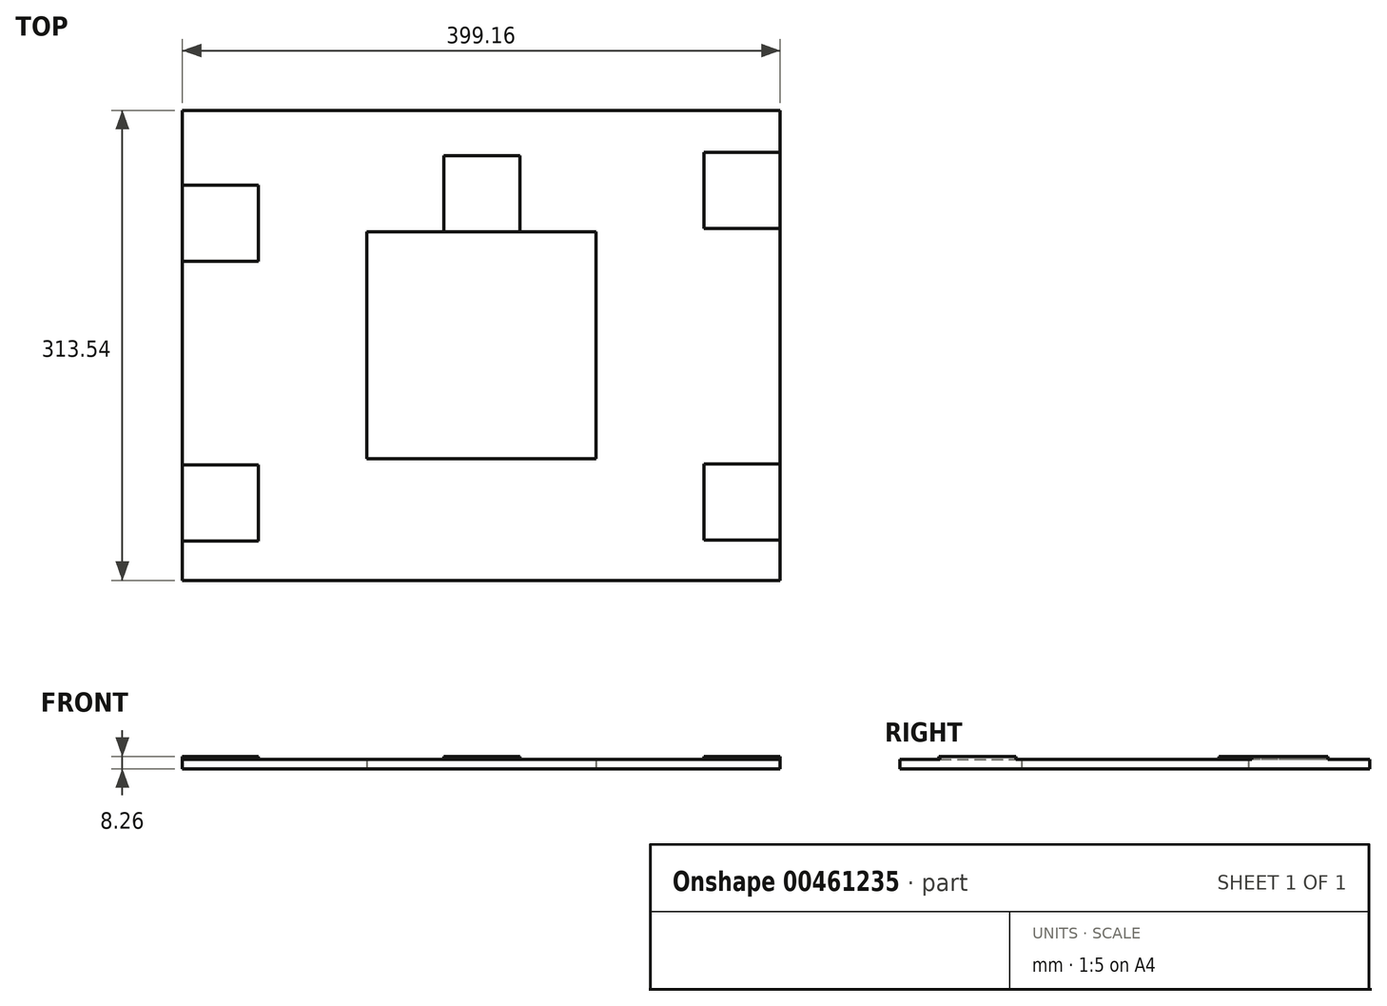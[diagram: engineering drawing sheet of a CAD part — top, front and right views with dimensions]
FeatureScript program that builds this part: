
annotation { "Feature Type Name" : "Feature", "Feature Type Description" : "" }
export const myFeature = defineFeature(function(context is Context, id is Id, definition is map)
    precondition{}
    {
        {
            var Q0;
            Q0=qCreatedBy(makeId("Top.planeOp"),FACE);
            var sketch = newSketch(context, id + "F0", { "sketchPlane" : qUnion([Q0])});
            skLineSegment(sketch, "E0.bottom", {"start": v(199.58, 156.77) * mm, "end": v(-199.58, 156.77) * mm});
            skLineSegment(sketch, "E0.top", {"start": v(199.58, -156.77) * mm, "end": v(-199.58, -156.77) * mm});
            skLineSegment(sketch, "E0.left", {"start": v(199.58, 156.77) * mm, "end": v(199.58, -156.77) * mm});
            skLineSegment(sketch, "E0.right", {"start": v(-199.58, 156.77) * mm, "end": v(-199.58, -156.77) * mm});
            skPoint(sketch, "E0.middle", {"position": v(0, 0) * mm});
            skLineSegment(sketch, "E1.bottom", {"start": v(76.5, 75.74) * mm, "end": v(-76.5, 75.74) * mm});
            skLineSegment(sketch, "E1.top", {"start": v(76.5, -75.74) * mm, "end": v(-76.5, -75.74) * mm});
            skLineSegment(sketch, "E1.left", {"start": v(76.5, 75.74) * mm, "end": v(76.5, -75.74) * mm});
            skLineSegment(sketch, "E1.right", {"start": v(-76.5, 75.74) * mm, "end": v(-76.5, -75.74) * mm});
            skSolve(sketch);
        }
        {
            var Q0;
            Q0=makeQuery(id+"F0.imprint","IMPRINT",FACE,{"disambiguationData":[TD([[makeQuery(id+"F0.imprint","IMPRINT",EDGE,{"derivedFrom":sQuery(id+"F0.wireOp",EDGE,"E0.bottom")}),1.0]])]});
            extrude(context, id + "F1", {"entities" : qUnion([Q0]), "depth" : 6.35 * mm});
        }
        {
            var Q0;
            Q0=makeQuery(id+"F1.opExtrude","CAP_FACE",FACE,{"disambiguationData":[OSD([sQuery(id+"F0.wireOp",EDGE,"E0.bottom"),sQuery(id+"F0.wireOp",EDGE,"E0.top"),sQuery(id+"F0.wireOp",EDGE,"E0.left"),sQuery(id+"F0.wireOp",EDGE,"E0.right"),sQuery(id+"F0.wireOp",EDGE,"E1.bottom"),sQuery(id+"F0.wireOp",EDGE,"E1.top"),sQuery(id+"F0.wireOp",EDGE,"E1.left"),sQuery(id+"F0.wireOp",EDGE,"E1.right")])],"isStart":false});
            var sketch = newSketch(context, id + "F2", { "sketchPlane" : qUnion([Q0])});
            skLineSegment(sketch, "E2.bottom", {"start": v(-199.58, 106.93) * mm, "end": v(-148.78, 106.93) * mm});
            skLineSegment(sketch, "E2.top", {"start": v(-199.58, 56.13) * mm, "end": v(-148.78, 56.13) * mm});
            skLineSegment(sketch, "E2.left", {"start": v(-199.58, 106.93) * mm, "end": v(-199.58, 56.13) * mm});
            skLineSegment(sketch, "E2.right", {"start": v(-148.78, 106.93) * mm, "end": v(-148.78, 56.13) * mm});
            skLineSegment(sketch, "E3.bottom", {"start": v(199.58, 128.8) * mm, "end": v(148.78, 128.8) * mm});
            skLineSegment(sketch, "E3.top", {"start": v(199.58, 78) * mm, "end": v(148.78, 78) * mm});
            skLineSegment(sketch, "E3.left", {"start": v(199.58, 128.8) * mm, "end": v(199.58, 78) * mm});
            skLineSegment(sketch, "E3.right", {"start": v(148.78, 128.8) * mm, "end": v(148.78, 78) * mm});
            skLineSegment(sketch, "E4.bottom", {"start": v(199.58, -130.05) * mm, "end": v(148.78, -130.05) * mm});
            skLineSegment(sketch, "E4.top", {"start": v(199.58, -79.25) * mm, "end": v(148.78, -79.25) * mm});
            skLineSegment(sketch, "E4.left", {"start": v(199.58, -130.05) * mm, "end": v(199.58, -79.25) * mm});
            skLineSegment(sketch, "E4.right", {"start": v(148.78, -130.05) * mm, "end": v(148.78, -79.25) * mm});
            skLineSegment(sketch, "E5.bottom", {"start": v(-199.58, -130.69) * mm, "end": v(-148.78, -130.69) * mm});
            skLineSegment(sketch, "E5.top", {"start": v(-199.58, -79.89) * mm, "end": v(-148.78, -79.89) * mm});
            skLineSegment(sketch, "E5.left", {"start": v(-199.58, -130.69) * mm, "end": v(-199.58, -79.89) * mm});
            skLineSegment(sketch, "E5.right", {"start": v(-148.78, -130.69) * mm, "end": v(-148.78, -79.89) * mm});
            skLineSegment(sketch, "E6.bottom", {"start": v(-25.13, 126.54) * mm, "end": v(25.67, 126.54) * mm});
            skLineSegment(sketch, "E6.top", {"start": v(-25.13, 75.74) * mm, "end": v(25.67, 75.74) * mm});
            skLineSegment(sketch, "E6.left", {"start": v(-25.13, 126.54) * mm, "end": v(-25.13, 75.74) * mm});
            skLineSegment(sketch, "E6.right", {"start": v(25.67, 126.54) * mm, "end": v(25.67, 75.74) * mm});
            skSolve(sketch);
        }
        {
            var Q0;
            Q0=makeQuery(id+"F2.imprint","IMPRINT",FACE,{"disambiguationData":[TD([[makeQuery(id+"F2.imprint","IMPRINT",EDGE,{"derivedFrom":sQuery(id+"F2.wireOp",EDGE,"E5.bottom")}),1.0]])]});
            var Q1;
            Q1=makeQuery(id+"F2.imprint","IMPRINT",FACE,{"disambiguationData":[TD([[makeQuery(id+"F2.imprint","IMPRINT",EDGE,{"derivedFrom":sQuery(id+"F2.wireOp",EDGE,"E2.bottom")}),-1.0]])]});
            var Q2;
            Q2=makeQuery(id+"F2.imprint","IMPRINT",FACE,{"disambiguationData":[TD([[makeQuery(id+"F2.imprint","IMPRINT",EDGE,{"derivedFrom":sQuery(id+"F2.wireOp",EDGE,"E6.bottom")}),-1.0]])]});
            var Q3;
            Q3=makeQuery(id+"F2.imprint","IMPRINT",FACE,{"disambiguationData":[TD([[makeQuery(id+"F2.imprint","IMPRINT",EDGE,{"derivedFrom":sQuery(id+"F2.wireOp",EDGE,"E3.bottom")}),1.0]])]});
            var Q4;
            Q4=makeQuery(id+"F2.imprint","IMPRINT",FACE,{"disambiguationData":[TD([[makeQuery(id+"F2.imprint","IMPRINT",EDGE,{"derivedFrom":sQuery(id+"F2.wireOp",EDGE,"E4.bottom")}),-1.0]])]});
            extrude(context, id + "F3", {"entities" : qUnion([Q0, Q1, Q2, Q3, Q4]), "operationType" : NewBodyOperationType.ADD, "depth" : 1.9 * mm});
        }
    });
